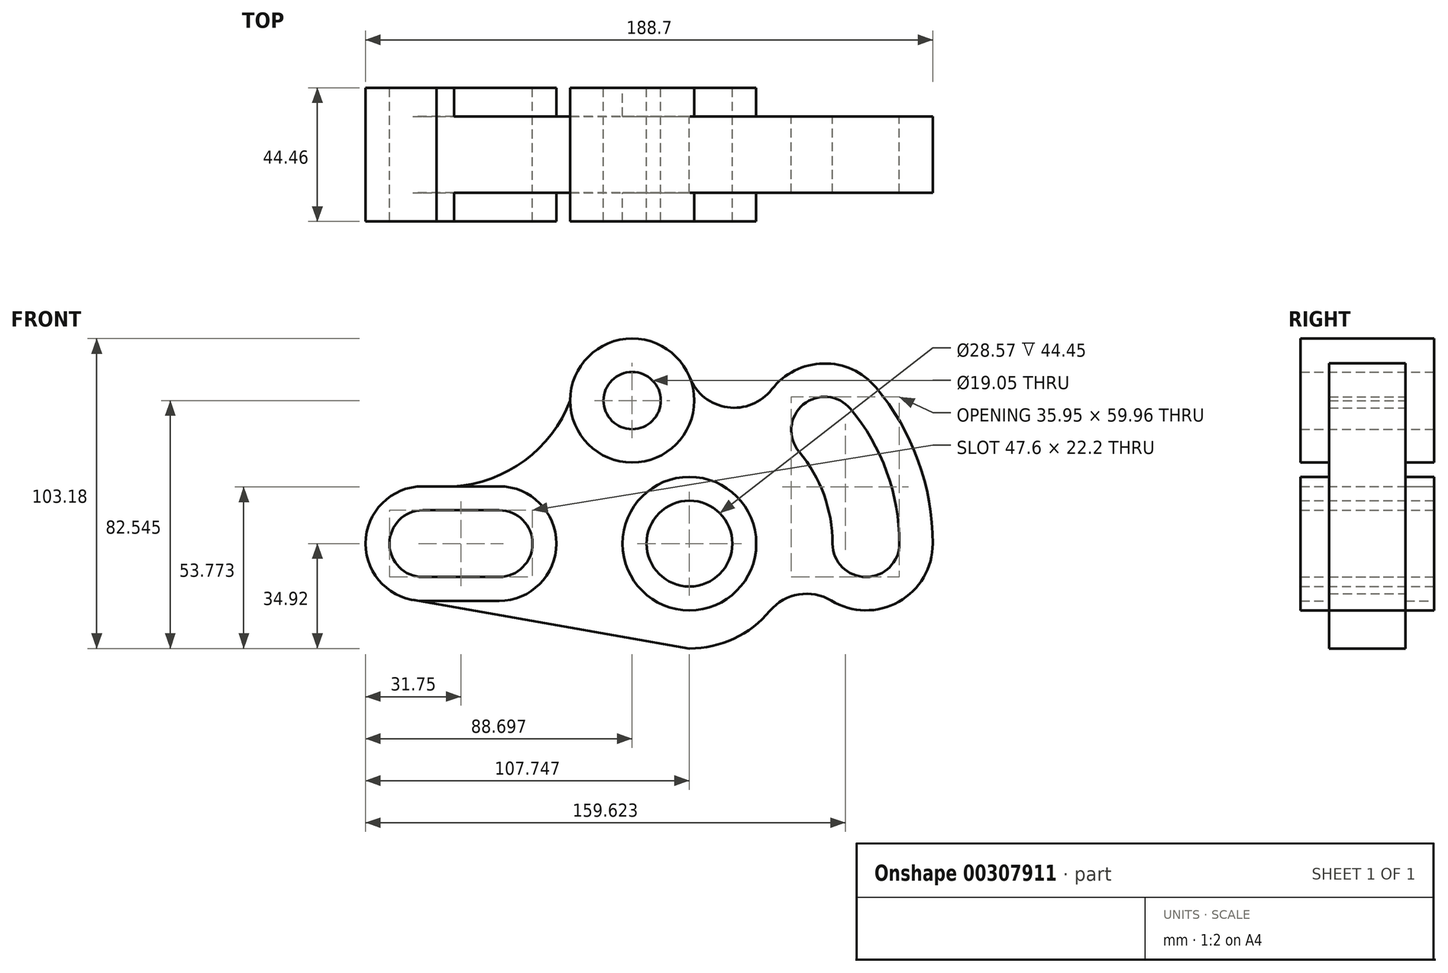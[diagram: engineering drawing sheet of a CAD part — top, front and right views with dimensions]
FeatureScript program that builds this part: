
annotation { "Feature Type Name" : "Feature", "Feature Type Description" : "" }
export const myFeature = defineFeature(function(context is Context, id is Id, definition is map)
    precondition{}
    {
        {
            var Q0;
            Q0=qCreatedBy(makeId("Front.planeOp"),FACE);
            var sketch = newSketch(context, id + "F0", { "sketchPlane" : qUnion([Q0])});
            skArc(sketch, "E0", {"start": v(0, 11.1) * mm, "mid": v(-11.1, 0) * mm, "end": v(0, -11.1) * mm});
            skArc(sketch, "E1", {"start": v(0, 19.05) * mm, "mid": v(-19.05, 0) * mm, "end": v(0, -19.05) * mm});
            skLineSegment(sketch, "E2", {"start": v(0, 11.1) * mm, "end": v(25.4, 11.1) * mm});
            skLineSegment(sketch, "E3", {"start": v(25.4, -11.1) * mm, "end": v(0, -11.1) * mm});
            skLineSegment(sketch, "E4", {"start": v(0, -19.05) * mm, "end": v(25.4, -19.05) * mm});
            skLineSegment(sketch, "E5", {"start": v(0, 19.05) * mm, "end": v(25.4, 19.05) * mm});
            skArc(sketch, "E6", {"start": v(25.4, -11.1) * mm, "mid": v(36.5, 0) * mm, "end": v(25.4, 11.1) * mm});
            skArc(sketch, "E7", {"start": v(25.4, -19.05) * mm, "mid": v(44.45, 0) * mm, "end": v(25.4, 19.05) * mm});
            skCircle(sketch, "E8", {"center": v(88.7, 0) * mm, "radius": 14.29 * mm});
            skCircle(sketch, "E9", {"center": v(88.7, 0) * mm, "radius": 22.23 * mm});
            skLineSegment(sketch, "E10", {"start": v(88.7, 0) * mm, "end": v(88.7, 47.62) * mm, "construction": true});
            skLineSegment(sketch, "E11", {"start": v(25.4, 0) * mm, "end": v(88.7, 0) * mm, "construction": true});
            skLineSegment(sketch, "E12", {"start": v(88.7, 47.62) * mm, "end": v(69.65, 47.62) * mm, "construction": true});
            skCircle(sketch, "E13", {"center": v(69.65, 47.62) * mm, "radius": 9.52 * mm});
            skCircle(sketch, "E14", {"center": v(69.65, 47.62) * mm, "radius": 20.64 * mm});
            skLineSegment(sketch, "E15", {"start": v(88.7, 0) * mm, "end": v(88.7, -34.92) * mm, "construction": true});
            skLineSegment(sketch, "E16", {"start": v(88.7, -34.92) * mm, "end": v(-3.3, -18.76) * mm});
            skLineSegment(sketch, "E17", {"start": v(88.7, 0) * mm, "end": v(147.42, 0) * mm, "construction": true});
            skArc(sketch, "E18", {"start": v(136.3, 0) * mm, "mid": v(147.42, -11.13) * mm, "end": v(158.55, 0) * mm});
            skLineSegment(sketch, "E19", {"start": v(88.7, 0) * mm, "end": v(133.68, 37.75) * mm, "construction": true});
            skArc(sketch, "E20", {"start": v(142.2, 44.9) * mm, "mid": v(126.53, 46.27) * mm, "end": v(125.16, 30.6) * mm});
            skArc(sketch, "E21.0", {"start": v(158.55, 0) * mm, "mid": v(154.33, 23.9) * mm, "end": v(142.2, 44.9) * mm});
            skArc(sketch, "E22.0", {"start": v(136.3, 0) * mm, "mid": v(133.43, 16.28) * mm, "end": v(125.16, 30.6) * mm});
            skArc(sketch, "E23", {"start": v(135.9, -19) * mm, "mid": v(158.33, -19.36) * mm, "end": v(169.65, 0) * mm});
            skArc(sketch, "E24", {"start": v(169.65, 0) * mm, "mid": v(164.76, 27.69) * mm, "end": v(150.7, 52.03) * mm});
            skArc(sketch, "E25.trimOffspring", {"start": v(150.7, 52.03) * mm, "mid": v(133.26, 59.97) * mm, "end": v(116.12, 51.37) * mm});
            skArc(sketch, "E26", {"start": v(4.56, 19.05) * mm, "mid": v(31.5, 26.02) * mm, "end": v(49, 47.63) * mm});
            skCircle(sketch, "E27", {"center": v(88.7, 0) * mm, "radius": 58.72 * mm, "construction": true});
            skArc(sketch, "E28", {"start": v(88.7, -34.92) * mm, "mid": v(103.49, -31.64) * mm, "end": v(115.5, -22.4) * mm});
            skArc(sketch, "E29", {"start": v(88.83, 55.24) * mm, "mid": v(101.6, 45.35) * mm, "end": v(116.42, 51.77) * mm});
            skArc(sketch, "E30", {"start": v(135.9, -19) * mm, "mid": v(125.07, -16.92) * mm, "end": v(115.5, -22.4) * mm});
            skArc(sketch, "E31.trimOffspring", {"start": v(88.7, 34.92) * mm, "mid": v(87.26, 34.9) * mm, "end": v(85.82, 34.8) * mm, "construction": true});
            skSolve(sketch);
        }
        {
            var Q0;
            {var subQ5=sQuery(id+"F0.wireOp",EDGE,"E4");Q0=makeQuery(id+"F0.imprint","IMPRINT",FACE,{"disambiguationData":[TD([[makeQuery(id+"F0.imprint","IMPRINT",EDGE,{"derivedFrom":subQ5}),-1.0]])]});}
            extrude(context, id + "F1", {"entities" : qUnion([Q0]), "endBound" : BoundingType.SYMMETRIC, "depth" : 25.4 * mm});
        }
        {
            var Q0;
            Q0=makeQuery(id+"F0.imprint","IMPRINT",FACE,{"disambiguationData":[TD([[makeQuery(id+"F0.imprint","IMPRINT",EDGE,{"derivedFrom":sQuery(id+"F0.wireOp",EDGE,"E0")}),-1.0]])]});
            var Q1;
            Q1=makeQuery(id+"F0.imprint","IMPRINT",FACE,{"disambiguationData":[TD([[makeQuery(id+"F0.imprint","IMPRINT",EDGE,{"derivedFrom":sQuery(id+"F0.wireOp",EDGE,"E13")}),-1.0]])]});
            var Q2;
            Q2=makeQuery(id+"F0.imprint","IMPRINT",FACE,{"disambiguationData":[TD([[makeQuery(id+"F0.imprint","IMPRINT",EDGE,{"derivedFrom":sQuery(id+"F0.wireOp",EDGE,"E8")}),-1.0]])]});
            extrude(context, id + "F2", {"entities" : qUnion([Q0, Q1, Q2]), "operationType" : NewBodyOperationType.ADD, "endBound" : BoundingType.SYMMETRIC, "depth" : 44.45 * mm});
        }
    });
